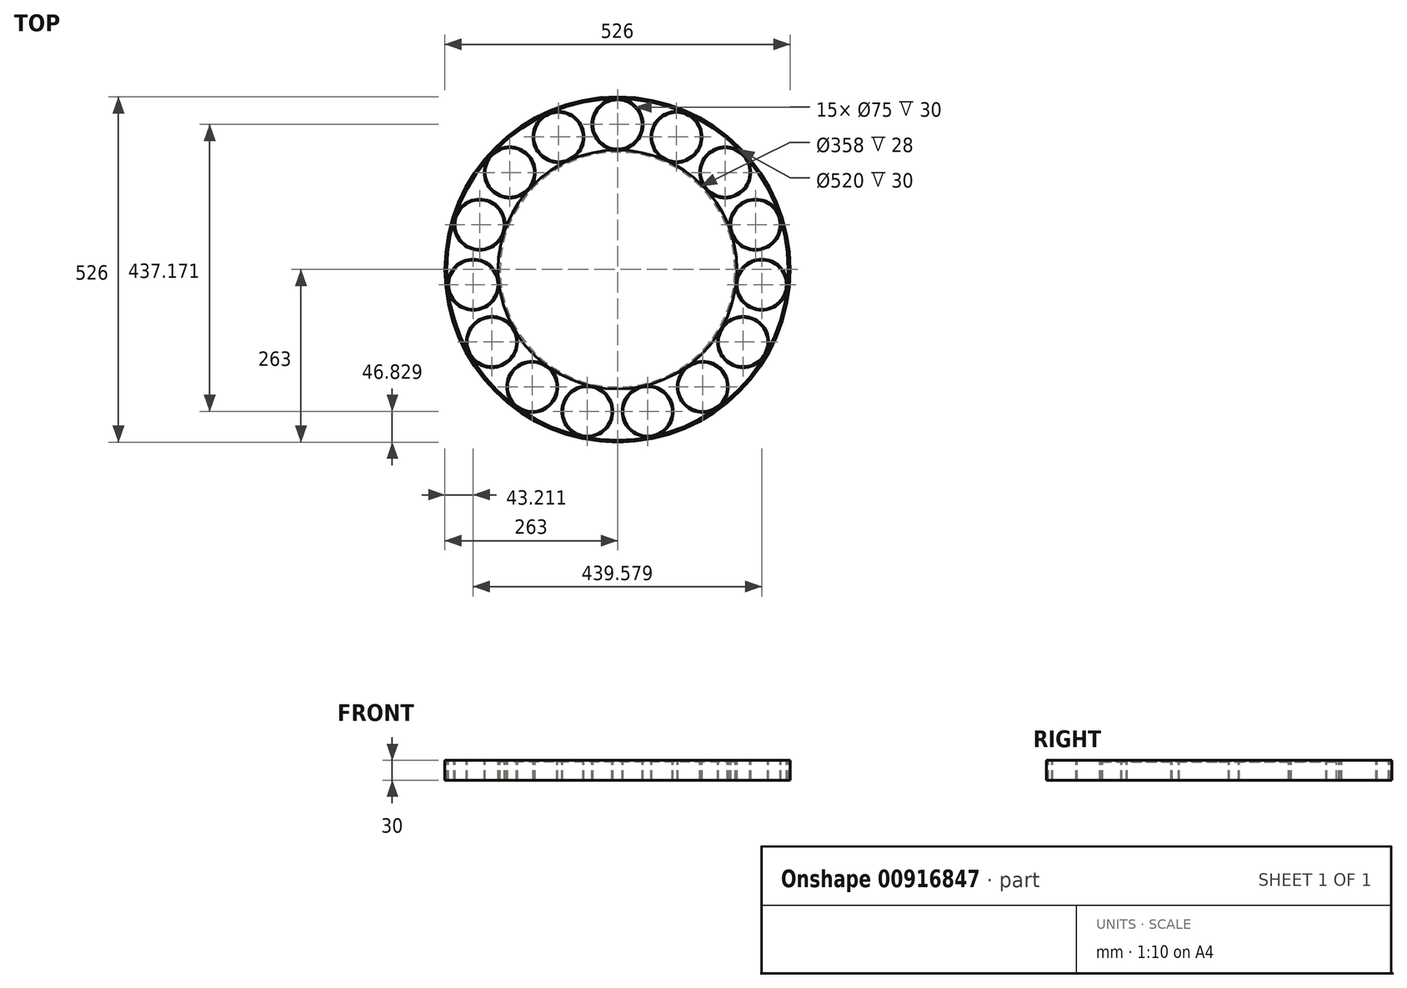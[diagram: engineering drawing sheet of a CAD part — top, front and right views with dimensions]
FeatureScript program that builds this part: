
annotation { "Feature Type Name" : "Feature", "Feature Type Description" : "" }
export const myFeature = defineFeature(function(context is Context, id is Id, definition is map)
    precondition{}
    {
        {
            var Q0;
            Q0=qCreatedBy(makeId("Top.planeOp"),FACE);
            var sketch = newSketch(context, id + "F0", { "sketchPlane" : qUnion([Q0])});
            skCircle(sketch, "E0", {"center": v(0, 0) * mm, "radius": 179 * mm});
            skCircle(sketch, "E1", {"center": v(0, 0) * mm, "radius": 182 * mm});
            skCircle(sketch, "E2", {"center": v(0, 0) * mm, "radius": 260 * mm});
            skCircle(sketch, "E3", {"center": v(0, 221) * mm, "radius": 39 * mm});
            skCircle(sketch, "E4", {"center": v(0, 221) * mm, "radius": 37.5 * mm});
            skCircle(sketch, "E5", {"center": v(0, 0) * mm, "radius": 263 * mm});
            skCircle(sketch, "E6.1.0", {"center": v(-89.89, 201.9) * mm, "radius": 37.5 * mm});
            skCircle(sketch, "E6.1.1", {"center": v(-89.89, 201.9) * mm, "radius": 39 * mm});
            skCircle(sketch, "E6.2.0", {"center": v(-164.24, 147.88) * mm, "radius": 37.5 * mm});
            skCircle(sketch, "E6.2.1", {"center": v(-164.24, 147.88) * mm, "radius": 39 * mm});
            skCircle(sketch, "E6.3.0", {"center": v(-210.18, 68.3) * mm, "radius": 37.5 * mm});
            skCircle(sketch, "E6.3.1", {"center": v(-210.18, 68.3) * mm, "radius": 39 * mm});
            skCircle(sketch, "E6.4.0", {"center": v(-219.79, -23.1) * mm, "radius": 37.5 * mm});
            skCircle(sketch, "E6.4.1", {"center": v(-219.79, -23.1) * mm, "radius": 39 * mm});
            skCircle(sketch, "E6.5.0", {"center": v(-191.4, -110.5) * mm, "radius": 37.5 * mm});
            skCircle(sketch, "E6.5.1", {"center": v(-191.4, -110.5) * mm, "radius": 39 * mm});
            skCircle(sketch, "E6.6.0", {"center": v(-129.9, -178.8) * mm, "radius": 37.5 * mm});
            skCircle(sketch, "E6.6.1", {"center": v(-129.9, -178.8) * mm, "radius": 39 * mm});
            skCircle(sketch, "E6.7.0", {"center": v(-45.95, -216.17) * mm, "radius": 37.5 * mm});
            skCircle(sketch, "E6.7.1", {"center": v(-45.95, -216.17) * mm, "radius": 39 * mm});
            skCircle(sketch, "E6.8.0", {"center": v(45.95, -216.17) * mm, "radius": 37.5 * mm});
            skCircle(sketch, "E6.8.1", {"center": v(45.95, -216.17) * mm, "radius": 39 * mm});
            skCircle(sketch, "E6.9.0", {"center": v(129.9, -178.8) * mm, "radius": 37.5 * mm});
            skCircle(sketch, "E6.9.1", {"center": v(129.9, -178.8) * mm, "radius": 39 * mm});
            skCircle(sketch, "E7.1.10.0", {"center": v(191.4, -110.5) * mm, "radius": 37.5 * mm});
            skCircle(sketch, "E7.2.10.0", {"center": v(191.4, -110.5) * mm, "radius": 39 * mm});
            skCircle(sketch, "E7.1.11.0", {"center": v(219.79, -23.1) * mm, "radius": 37.5 * mm});
            skCircle(sketch, "E7.2.11.0", {"center": v(219.79, -23.1) * mm, "radius": 39 * mm});
            skCircle(sketch, "E7.1.12.0", {"center": v(210.18, 68.3) * mm, "radius": 37.5 * mm});
            skCircle(sketch, "E7.2.12.0", {"center": v(210.18, 68.3) * mm, "radius": 39 * mm});
            skCircle(sketch, "E7.1.13.0", {"center": v(164.24, 147.88) * mm, "radius": 37.5 * mm});
            skCircle(sketch, "E7.2.13.0", {"center": v(164.24, 147.88) * mm, "radius": 39 * mm});
            skCircle(sketch, "E7.1.14.0", {"center": v(89.89, 201.9) * mm, "radius": 37.5 * mm});
            skCircle(sketch, "E7.2.14.0", {"center": v(89.89, 201.9) * mm, "radius": 39 * mm});
            skSolve(sketch);
        }
        {
            var Q0;
            Q0=qSketchRegion(id+"F0",true);
            var Q1;
            Q1=makeQuery(id+"F0.imprint","IMPRINT",FACE,{"disambiguationData":[TD([[makeQuery(id+"F0.imprint","IMPRINT",EDGE,{"derivedFrom":sQuery(id+"F0.wireOp",EDGE,"E0")}),-1.0]])]});
            var Q2;
            Q2=makeQuery(id+"F0.imprint","IMPRINT",FACE,{"disambiguationData":[TD([[makeQuery(id+"F0.imprint","IMPRINT",EDGE,{"derivedFrom":sQuery(id+"F0.wireOp",EDGE,"E6.7.0")}),-1.0]])]});
            var Q3;
            Q3=makeQuery(id+"F0.imprint","IMPRINT",FACE,{"disambiguationData":[TD([[makeQuery(id+"F0.imprint","IMPRINT",EDGE,{"derivedFrom":sQuery(id+"F0.wireOp",EDGE,"E6.6.0")}),-1.0]])]});
            var Q4;
            Q4=makeQuery(id+"F0.imprint","IMPRINT",FACE,{"disambiguationData":[TD([[makeQuery(id+"F0.imprint","IMPRINT",EDGE,{"derivedFrom":sQuery(id+"F0.wireOp",EDGE,"E6.5.0")}),-1.0]])]});
            var Q5;
            Q5=makeQuery(id+"F0.imprint","IMPRINT",FACE,{"disambiguationData":[TD([[makeQuery(id+"F0.imprint","IMPRINT",EDGE,{"derivedFrom":sQuery(id+"F0.wireOp",EDGE,"E6.4.0")}),-1.0]])]});
            var Q6;
            Q6=makeQuery(id+"F0.imprint","IMPRINT",FACE,{"disambiguationData":[TD([[makeQuery(id+"F0.imprint","IMPRINT",EDGE,{"derivedFrom":sQuery(id+"F0.wireOp",EDGE,"E6.3.0")}),-1.0]])]});
            var Q7;
            Q7=makeQuery(id+"F0.imprint","IMPRINT",FACE,{"disambiguationData":[TD([[makeQuery(id+"F0.imprint","IMPRINT",EDGE,{"derivedFrom":sQuery(id+"F0.wireOp",EDGE,"E6.2.0")}),-1.0]])]});
            var Q8;
            Q8=makeQuery(id+"F0.imprint","IMPRINT",FACE,{"disambiguationData":[TD([[makeQuery(id+"F0.imprint","IMPRINT",EDGE,{"derivedFrom":sQuery(id+"F0.wireOp",EDGE,"E6.1.0")}),-1.0]])]});
            var Q9;
            Q9=makeQuery(id+"F0.imprint","IMPRINT",FACE,{"disambiguationData":[TD([[makeQuery(id+"F0.imprint","IMPRINT",EDGE,{"derivedFrom":sQuery(id+"F0.wireOp",EDGE,"E4")}),-1.0]])]});
            var Q10;
            Q10=makeQuery(id+"F0.imprint","IMPRINT",FACE,{"disambiguationData":[TD([[makeQuery(id+"F0.imprint","IMPRINT",EDGE,{"derivedFrom":sQuery(id+"F0.wireOp",EDGE,"E6.9.0")}),-1.0]])]});
            var Q11;
            Q11=makeQuery(id+"F0.imprint","IMPRINT",FACE,{"disambiguationData":[TD([[makeQuery(id+"F0.imprint","IMPRINT",EDGE,{"derivedFrom":sQuery(id+"F0.wireOp",EDGE,"E6.8.0")}),-1.0]])]});
            var Q12;
            Q12=makeQuery(id+"F0.imprint","IMPRINT",FACE,{"disambiguationData":[TD([[makeQuery(id+"F0.imprint","IMPRINT",EDGE,{"derivedFrom":sQuery(id+"F0.wireOp",EDGE,"E7.1.14.0")}),-1.0]])]});
            var Q13;
            Q13=makeQuery(id+"F0.imprint","IMPRINT",FACE,{"disambiguationData":[TD([[makeQuery(id+"F0.imprint","IMPRINT",EDGE,{"derivedFrom":sQuery(id+"F0.wireOp",EDGE,"E7.1.13.0")}),-1.0]])]});
            var Q14;
            Q14=makeQuery(id+"F0.imprint","IMPRINT",FACE,{"disambiguationData":[TD([[makeQuery(id+"F0.imprint","IMPRINT",EDGE,{"derivedFrom":sQuery(id+"F0.wireOp",EDGE,"E7.1.12.0")}),-1.0]])]});
            var Q15;
            Q15=makeQuery(id+"F0.imprint","IMPRINT",FACE,{"disambiguationData":[TD([[makeQuery(id+"F0.imprint","IMPRINT",EDGE,{"derivedFrom":sQuery(id+"F0.wireOp",EDGE,"E7.1.11.0")}),-1.0]])]});
            var Q16;
            Q16=makeQuery(id+"F0.imprint","IMPRINT",FACE,{"disambiguationData":[TD([[makeQuery(id+"F0.imprint","IMPRINT",EDGE,{"derivedFrom":sQuery(id+"F0.wireOp",EDGE,"E7.1.10.0")}),-1.0]])]});
            extrude(context, id + "F1", {"entities" : qUnion([Q0, Q1, Q2, Q3, Q4, Q5, Q6, Q7, Q8, Q9, Q10, Q11, Q12, Q13, Q14, Q15, Q16]), "oppositeDirection" : true, "depth" : 30 * mm, "offsetDistance" : 25 * mm});
        }
        {
            var Q0;
            Q0=qCreatedBy(makeId("Top.planeOp"),FACE);
            var sketch = newSketch(context, id + "F2", { "sketchPlane" : qUnion([Q0])});
            skCircle(sketch, "E8", {"center": v(0, 0) * mm, "radius": 179 * mm});
            skSolve(sketch);
        }
        {
            var Q0;
            Q0=qSketchRegion(id+"F2",true);
            extrude(context, id + "F3", {"entities" : qUnion([Q0]), "operationType" : NewBodyOperationType.ADD, "oppositeDirection" : true, "depth" : 2 * mm, "offsetDistance" : 25 * mm});
        }
    });
